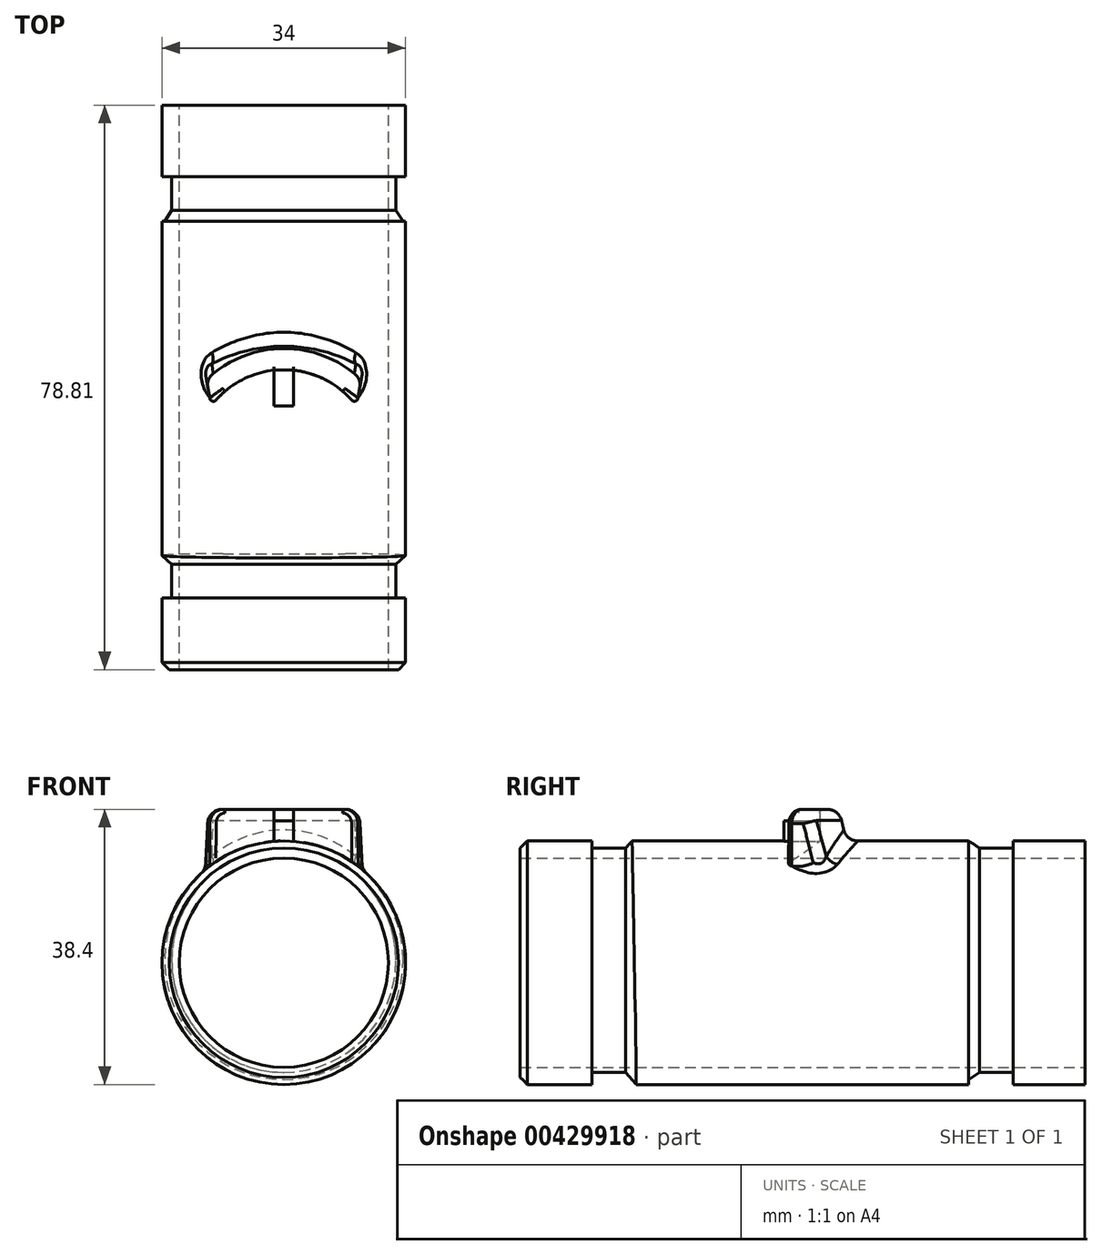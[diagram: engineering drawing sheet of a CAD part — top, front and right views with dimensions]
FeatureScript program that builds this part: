
annotation { "Feature Type Name" : "Feature", "Feature Type Description" : "" }
export const myFeature = defineFeature(function(context is Context, id is Id, definition is map)
    precondition{}
    {
        {
            var Q0;
            Q0=qCreatedBy(makeId("Front.planeOp"),FACE);
            var sketch = newSketch(context, id + "F0", { "sketchPlane" : qUnion([Q0])});
            skCircle(sketch, "E0", {"center": v(0, 0) * mm, "radius": 17 * mm});
            skCircle(sketch, "E1", {"center": v(0, 0) * mm, "radius": 14.6 * mm});
            skSolve(sketch);
        }
        {
            var Q0;
            Q0=makeQuery(id+"F0.imprint","IMPRINT",FACE,{"disambiguationData":[TD([[makeQuery(id+"F0.imprint","IMPRINT",EDGE,{"derivedFrom":sQuery(id+"F0.wireOp",EDGE,"E0")}),1.0]])]});
            extrude(context, id + "F1", {"entities" : qUnion([Q0]), "depth" : 83.8 * mm - 5 * mm});
        }
        {
            var Q0;
            Q0=makeQuery(id+"F1.opExtrude","CAP_FACE",FACE,{"disambiguationData":[OSD([sQuery(id+"F0.wireOp",EDGE,"E0"),sQuery(id+"F0.wireOp",EDGE,"E1")])],"isStart":true});
            cPlane(context, id + "F2", {"entities" : qUnion([Q0]), "cplaneType" : CPlaneType.OFFSET, "offset" : 10 * mm, "oppositeDirection" : true, "width" : 150 * mm, "height" : 150 * mm});
        }
        {
            var Q0;
            Q0=qCreatedBy(id+"F2.planeOp",FACE);
            var sketch = newSketch(context, id + "F3", { "sketchPlane" : qUnion([Q0])});
            skCircle(sketch, "E2.0", {"center": v(0, 0) * mm, "radius": 17 * mm});
            skCircle(sketch, "E3", {"center": v(0, 0.35) * mm, "radius": 15.65 * mm});
            skSolve(sketch);
        }
        {
            var Q0;
            Q0=qSketchRegion(id+"F3",true);
            extrude(context, id + "F4", {"entities" : qUnion([Q0]), "operationType" : NewBodyOperationType.REMOVE, "oppositeDirection" : true, "depth" : 6.2 * mm});
        }
        {
            var Q0;
            Q0=makeQuery(id+"F4.boolean.opBoolean","COPY",EDGE,{"derivedFrom":makeQuery(id+"F4.opExtrude","CAP_EDGE",EDGE,{"disambiguationData":[OSD([sQuery(id+"F3.wireOp",EDGE,"E3")])],"isStart":false})});
            chamfer(context, id + "F5", {"entities" : qUnion([Q0]), "chamferType" : ChamferType.TWO_OFFSETS, "width1" : 1.5 * mm, "oppositeDirection" : false, "width2" : 1 * mm, "tangentPropagation" : true});
        }
        {
            var Q0;
            Q0=makeQuery(id+"F1.opExtrude","CAP_FACE",FACE,{"disambiguationData":[OSD([sQuery(id+"F0.wireOp",EDGE,"E0"),sQuery(id+"F0.wireOp",EDGE,"E1")])],"isStart":true});
            cPlane(context, id + "F6", {"entities" : qUnion([Q0]), "cplaneType" : CPlaneType.OFFSET, "offset" : 37 * mm, "oppositeDirection" : true, "width" : 150 * mm, "height" : 150 * mm});
        }
        {
            var Q0;
            Q0=qCreatedBy(id+"F6.planeOp",FACE);
            var sketch = newSketch(context, id + "F7", { "sketchPlane" : qUnion([Q0])});
            skLineSegment(sketch, "E4", {"start": v(0, 0) * mm, "end": v(0, 19.8) * mm, "construction": true});
            skLineSegment(sketch, "E5.rect.bottom", {"start": v(1.35, 19.8) * mm, "end": v(-1.35, 19.8) * mm});
            skLineSegment(sketch, "E5.rect.top", {"start": v(1.35, 15.77) * mm, "end": v(-1.35, 15.77) * mm});
            skLineSegment(sketch, "E5.rect.left", {"start": v(1.35, 19.8) * mm, "end": v(1.35, 15.77) * mm});
            skLineSegment(sketch, "E5.rect.right", {"start": v(-1.35, 19.8) * mm, "end": v(-1.35, 15.77) * mm});
            skPoint(sketch, "E5.rect.middle", {"position": v(0, 17.79) * mm});
            skCircle(sketch, "E6.0", {"center": v(0, 0) * mm, "radius": 17 * mm, "construction": true});
            skSolve(sketch);
        }
        {
            var Q0;
            Q0=qSketchRegion(id+"F7",true);
            extrude(context, id + "F8", {"entities" : qUnion([Q0]), "operationType" : NewBodyOperationType.ADD, "oppositeDirection" : true, "depth" : 5 * mm});
        }
        {
            var Q0;
            Q0=makeQuery(id+"F8.opExtrude","SWEPT_FACE",FACE,{"disambiguationData":[OSD([sQuery(id+"F7.wireOp",EDGE,"E5.rect.bottom")])]});
            cPlane(context, id + "F9", {"entities" : qUnion([Q0]), "cplaneType" : CPlaneType.OFFSET, "offset" : 1.6 * mm, "width" : 150 * mm, "height" : 150 * mm});
        }
        {
            var Q0;
            Q0=qCreatedBy(id+"F9.planeOp",FACE);
            cPlane(context, id + "F10", {"entities" : qUnion([Q0]), "cplaneType" : CPlaneType.OFFSET, "offset" : 8.8 * mm, "oppositeDirection" : true, "width" : 150 * mm, "height" : 150 * mm});
        }
        {
            var Q0;
            Q0=qCreatedBy(id+"F9.planeOp",FACE);
            var sketch = newSketch(context, id + "F11", { "sketchPlane" : qUnion([Q0])});
            skArc(sketch, "E7", {"start": v(10.7, -38.69) * mm, "mid": v(0, -34.33) * mm, "end": v(-10.7, -38.69) * mm});
            skArc(sketch, "E8", {"start": v(-1.35, -37) * mm, "mid": v(-6.27, -38.58) * mm, "end": v(-10.15, -42) * mm});
            skLineSegment(sketch, "E9", {"start": v(1.35, -42) * mm, "end": v(10.15, -42) * mm, "construction": true});
            skPoint(sketch, "E10.0", {"position": v(1.35, -42) * mm});
            skLineSegment(sketch, "E10.2", {"start": v(1.35, -42) * mm, "end": v(1.35, -37) * mm, "construction": true});
            skLineSegment(sketch, "E11.0", {"start": v(-1.35, -37) * mm, "end": v(1.35, -37) * mm});
            skArc(sketch, "E12.trimOffspring", {"start": v(10.15, -42) * mm, "mid": v(6.27, -38.58) * mm, "end": v(1.35, -37) * mm});
            skLineSegment(sketch, "E13", {"start": v(-10.15, -42) * mm, "end": v(-10.7, -38.69) * mm});
            skLineSegment(sketch, "E14", {"start": v(0, -42) * mm, "end": v(0, -34.33) * mm, "construction": true});
            skLineSegment(sketch, "E15.0.MirrorCS", {"start": v(-19.77, -45.22) * mm, "end": v(-22.21, -37.95) * mm, "construction": true});
            skLineSegment(sketch, "E16.0.MirrorCS", {"start": v(10.15, -42) * mm, "end": v(10.7, -38.69) * mm});
            skSolve(sketch);
        }
        {
            var Q0;
            Q0=qCreatedBy(id+"F10.planeOp",FACE);
            var sketch = newSketch(context, id + "F12", { "sketchPlane" : qUnion([Q0])});
            skArc(sketch, "E17.0", {"start": v(-1.35, -37) * mm, "mid": v(-6.27, -38.58) * mm, "end": v(-10.15, -42) * mm});
            skLineSegment(sketch, "E18", {"start": v(-10.15, -42) * mm, "end": v(-11.17, -36.3) * mm});
            skArc(sketch, "E19", {"start": v(11.17, -36.3) * mm, "mid": v(0, -32.23) * mm, "end": v(-11.17, -36.3) * mm});
            skLineSegment(sketch, "E20", {"start": v(0, -42.05) * mm, "end": v(0, -34.3) * mm, "construction": true});
            skLineSegment(sketch, "E21.0.MirrorCS", {"start": v(10.15, -42) * mm, "end": v(11.17, -36.3) * mm});
            skArc(sketch, "E22.0.MirrorCS", {"start": v(1.35, -37) * mm, "mid": v(6.27, -38.58) * mm, "end": v(10.15, -42) * mm});
            skLineSegment(sketch, "E23", {"start": v(-1.35, -37) * mm, "end": v(1.35, -37) * mm});
            skSolve(sketch);
        }
        {
            var Q1;
            Q1=makeQuery(id+"F11.imprint","IMPRINT",FACE,{"disambiguationData":[TD([[makeQuery(id+"F11.imprint","IMPRINT",EDGE,{"derivedFrom":sQuery(id+"F11.wireOp",EDGE,"E7")}),1.0]])]});
            var Q2;
            Q2=qSketchRegion(id+"F12",true);
            loft(context, id + "F13", {"operationType" : NewBodyOperationType.ADD, "sheetProfilesArray" : [{ "sheetProfileEntities" : qUnion([Q1]) }, { "sheetProfileEntities" : qUnion([Q2]) }]});
        }
        {
            var Q0;
            Q0=makeQuery(id+"F1.opExtrude","CAP_FACE",FACE,{"disambiguationData":[OSD([sQuery(id+"F0.wireOp",EDGE,"E0"),sQuery(id+"F0.wireOp",EDGE,"E1")])],"isStart":false});
            var sketch = newSketch(context, id + "F14", { "sketchPlane" : qUnion([Q0])});
            skCircle(sketch, "E24.0", {"center": v(0, 0) * mm, "radius": 14.6 * mm});
            skSolve(sketch);
        }
        {
            var Q0;
            Q0=qSketchRegion(id+"F14",true);
            extrude(context, id + "F15", {"entities" : qUnion([Q0]), "operationType" : NewBodyOperationType.REMOVE, "oppositeDirection" : true, "depth" : 57.04 * mm});
        }
        {
            var Q0;
            Q0=makeQuery(id+"F1.opExtrude","CAP_FACE",FACE,{"disambiguationData":[OSD([sQuery(id+"F0.wireOp",EDGE,"E0"),sQuery(id+"F0.wireOp",EDGE,"E1")])],"isStart":false});
            cPlane(context, id + "F16", {"entities" : qUnion([Q0]), "cplaneType" : CPlaneType.OFFSET, "offset" : 10 * mm, "oppositeDirection" : true, "width" : 150 * mm, "height" : 150 * mm});
        }
        {
            var Q0;
            Q0=qCreatedBy(id+"F16.planeOp",FACE);
            var sketch = newSketch(context, id + "F17", { "sketchPlane" : qUnion([Q0])});
            skCircle(sketch, "E25.0", {"center": v(0, 0) * mm, "radius": 17 * mm});
            skCircle(sketch, "E26", {"center": v(0, 0.35) * mm, "radius": 15.65 * mm});
            skSolve(sketch);
        }
        {
            var Q0;
            Q0=qSketchRegion(id+"F17",true);
            extrude(context, id + "F18", {"entities" : qUnion([Q0]), "operationType" : NewBodyOperationType.REMOVE, "oppositeDirection" : true, "depth" : 6.2 * mm});
        }
        {
            var Q0;
            Q0=makeQuery(id+"F18.boolean.opBoolean","COPY",EDGE,{"derivedFrom":makeQuery(id+"F18.opExtrude","CAP_EDGE",EDGE,{"disambiguationData":[OSD([sQuery(id+"F17.wireOp",EDGE,"E26")])],"isStart":false})});
            chamfer(context, id + "F19", {"entities" : qUnion([Q0]), "chamferType" : ChamferType.TWO_OFFSETS, "width1" : 1.5 * mm, "oppositeDirection" : false, "width2" : 1.65 * mm, "tangentPropagation" : true});
        }
        {
            var Q0;
            Q0=makeQuery(id+"F13.opLoft","SWEPT_EDGE",EDGE,{"disambiguationData":[OSD([sQuery(id+"F11.wireOp",EDGE,"E7"),sQuery(id+"F11.wireOp",EDGE,"E13"),sQuery(id+"F12.wireOp",EDGE,"E18"),sQuery(id+"F12.wireOp",EDGE,"E19")])]});
            var Q1;
            Q1=makeQuery(id+"F13.opLoft","SWEPT_EDGE",EDGE,{"disambiguationData":[OSD([sQuery(id+"F11.wireOp",EDGE,"E7"),sQuery(id+"F11.wireOp",EDGE,"E16.0.MirrorCS"),sQuery(id+"F12.wireOp",EDGE,"E19"),sQuery(id+"F12.wireOp",EDGE,"E21.0.MirrorCS")])]});
            var Q2;
            {var subQ0=sQuery(id+"F0.wireOp",EDGE,"E0");Q2=makeQuery(id+"F13.boolean.opBoolean","INTERSECT",EDGE,{"derivedFrom":[makeQuery(id+"F4.boolean.opBoolean","SPLIT",FACE,{"disambiguationData":[TD([makeQuery(id+"F1.opExtrude","CAP_FACE",FACE,{"disambiguationData":[OSD([subQ0,sQuery(id+"F0.wireOp",EDGE,"E1")])],"isStart":false})])],"derivedFrom":makeQuery(id+"F1.opExtrude","SWEPT_FACE",FACE,{"disambiguationData":[OSD([subQ0])]})}),makeQuery(id+"F13.opLoft","SWEPT_FACE",FACE,{"disambiguationData":[OSD([sQuery(id+"F11.wireOp",EDGE,"E7"),sQuery(id+"F11.wireOp",EDGE,"E13"),sQuery(id+"F11.wireOp",EDGE,"E16.0.MirrorCS"),sQuery(id+"F12.wireOp",EDGE,"E18"),sQuery(id+"F12.wireOp",EDGE,"E19"),sQuery(id+"F12.wireOp",EDGE,"E21.0.MirrorCS")])]})]});}
            var Q3;
            Q3=makeQuery(id+"F13.opLoft","MID_CAP_EDGE",EDGE,{"disambiguationData":[OSD([sQuery(id+"F11.wireOp",EDGE,"E7"),sQuery(id+"F11.wireOp",EDGE,"E13"),sQuery(id+"F11.wireOp",EDGE,"E16.0.MirrorCS")])],"capPos":0.0});
            var Q4;
            Q4=makeQuery(id+"F13.opLoft","MID_CAP_EDGE",EDGE,{"disambiguationData":[OSD([sQuery(id+"F11.wireOp",EDGE,"E7"),sQuery(id+"F11.wireOp",EDGE,"E12.trimOffspring"),sQuery(id+"F11.wireOp",EDGE,"E16.0.MirrorCS")])],"capPos":0.0});
            var Q5;
            Q5=makeQuery(id+"F13.opLoft","MID_CAP_EDGE",EDGE,{"disambiguationData":[OSD([sQuery(id+"F11.wireOp",EDGE,"E7"),sQuery(id+"F11.wireOp",EDGE,"E8"),sQuery(id+"F11.wireOp",EDGE,"E13")])],"capPos":0.0});
            fillet(context, id + "F20", {"entities" : qUnion([Q0, Q1, Q2, Q3, Q4, Q5]), "radius" : 2 * mm, "tangentPropagation" : true, "allowEdgeOverflow" : false});
        }
        {
            var Q0;
            Q0=makeQuery(id+"F1.opExtrude","CAP_EDGE",EDGE,{"disambiguationData":[OSD([sQuery(id+"F0.wireOp",EDGE,"E0")])],"isStart":false});
            chamfer(context, id + "F21", {"entities" : qUnion([Q0]), "width" : 1 * mm, "tangentPropagation" : true});
        }
        {
            var Q0;
            Q0=makeQuery(id+"F13.opLoft","SWEPT_EDGE",EDGE,{"disambiguationData":[OSD([sQuery(id+"F11.wireOp",EDGE,"E8"),sQuery(id+"F11.wireOp",EDGE,"E13"),sQuery(id+"F12.wireOp",EDGE,"E17.0"),sQuery(id+"F12.wireOp",EDGE,"E18")])]});
            var Q1;
            Q1=makeQuery(id+"F13.opLoft","SWEPT_EDGE",EDGE,{"disambiguationData":[OSD([sQuery(id+"F11.wireOp",EDGE,"E12.trimOffspring"),sQuery(id+"F11.wireOp",EDGE,"E16.0.MirrorCS"),sQuery(id+"F12.wireOp",EDGE,"E21.0.MirrorCS"),sQuery(id+"F12.wireOp",EDGE,"E22.0.MirrorCS")])]});
            var Q2;
            Q2=makeQuery(id+"F13.opLoft","MID_CAP_EDGE",EDGE,{"disambiguationData":[OSD([sQuery(id+"F11.wireOp",EDGE,"E8"),sQuery(id+"F11.wireOp",EDGE,"E11.0"),sQuery(id+"F11.wireOp",EDGE,"E12.trimOffspring")])],"capPos":0.0});
            fillet(context, id + "F22", {"entities" : qUnion([Q0, Q1, Q2]), "radius" : .5 * mm, "tangentPropagation" : true, "allowEdgeOverflow" : false});
        }
    });
